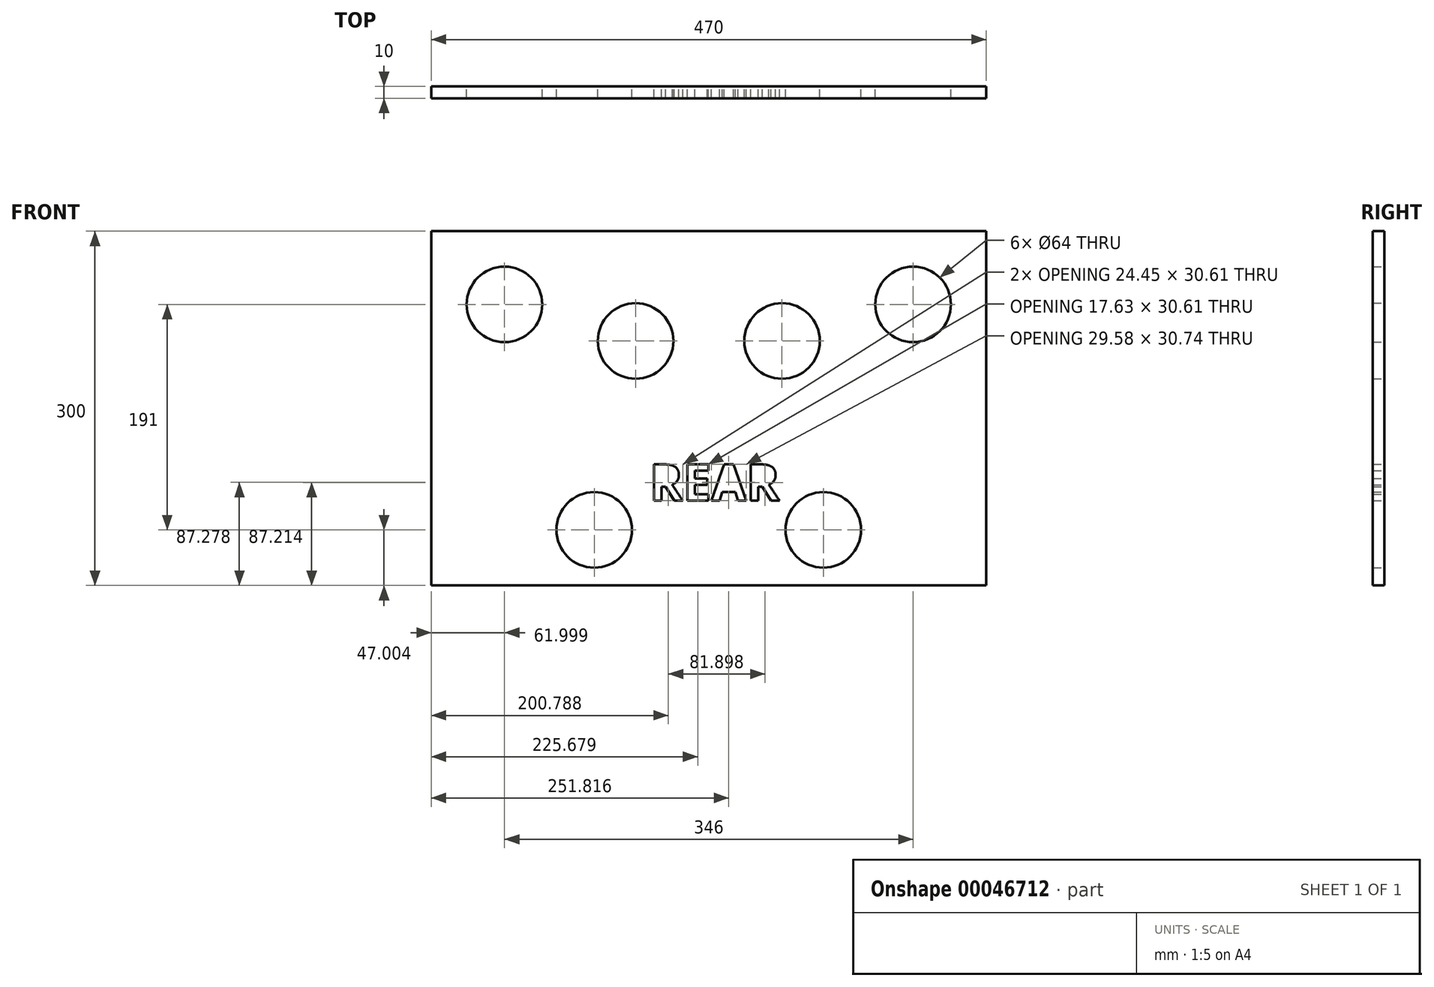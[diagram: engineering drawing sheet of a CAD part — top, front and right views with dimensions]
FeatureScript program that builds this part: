
annotation { "Feature Type Name" : "Feature", "Feature Type Description" : "" }
export const myFeature = defineFeature(function(context is Context, id is Id, definition is map)
    precondition{}
    {
        {
            var Q0;
            Q0=qCreatedBy(makeId("Front.planeOp"),FACE);
            var sketch = newSketch(context, id + "F0", { "sketchPlane" : qUnion([Q0])});
            skLineSegment(sketch, "E0.bottom", {"start": v(-236.5, 149.52) * mm, "end": v(233.5, 149.52) * mm});
            skLineSegment(sketch, "E0.top", {"start": v(-236.5, -150.48) * mm, "end": v(233.5, -150.48) * mm});
            skLineSegment(sketch, "E0.left", {"start": v(-236.5, 149.52) * mm, "end": v(-236.5, -150.48) * mm});
            skLineSegment(sketch, "E0.right", {"start": v(233.5, 149.52) * mm, "end": v(233.5, -150.48) * mm});
            skLineSegment(sketch, "E1", {"start": v(-1.5, 169.67) * mm, "end": v(-1.5, -190.98) * mm, "construction": true});
            skLineSegment(sketch, "E2", {"start": v(-294.39, -5.48) * mm, "end": v(295.29, -5.48) * mm, "construction": true});
            skCircle(sketch, "E3", {"center": v(171.5, 87.52) * mm, "radius": 32 * mm});
            skCircle(sketch, "E4", {"center": v(60.5, 56.52) * mm, "radius": 32 * mm});
            skCircle(sketch, "E5", {"center": v(95.5, -103.48) * mm, "radius": 32 * mm});
            skCircle(sketch, "E6", {"center": v(-98.5, -103.48) * mm, "radius": 32 * mm});
            skCircle(sketch, "E7", {"center": v(-63.5, 56.52) * mm, "radius": 32 * mm});
            skCircle(sketch, "E8", {"center": v(-174.5, 87.52) * mm, "radius": 32 * mm});
            skText(sketch, "E9", { "text": "REAR", "fontName": "OpenSans-Bold.ttf"});
            const initialGuessF0  = {"E9": [-0.05179, -0.07857, 1, 0, 0.03087]};
            skSetInitialGuess(sketch, initialGuessF0);
            skSolve(sketch);
        }
        {
            var Q0;
            Q0=makeQuery(id+"F0.imprint","IMPRINT",FACE,{"disambiguationData":[TD([[makeQuery(id+"F0.imprint","IMPRINT",EDGE,{"derivedFrom":sQuery(id+"F0.wireOp",EDGE,"E0.bottom")}),-1.0]])]});
            extrude(context, id + "F1", {"entities" : qUnion([Q0]), "depth" : 10 * mm});
        }
    });
